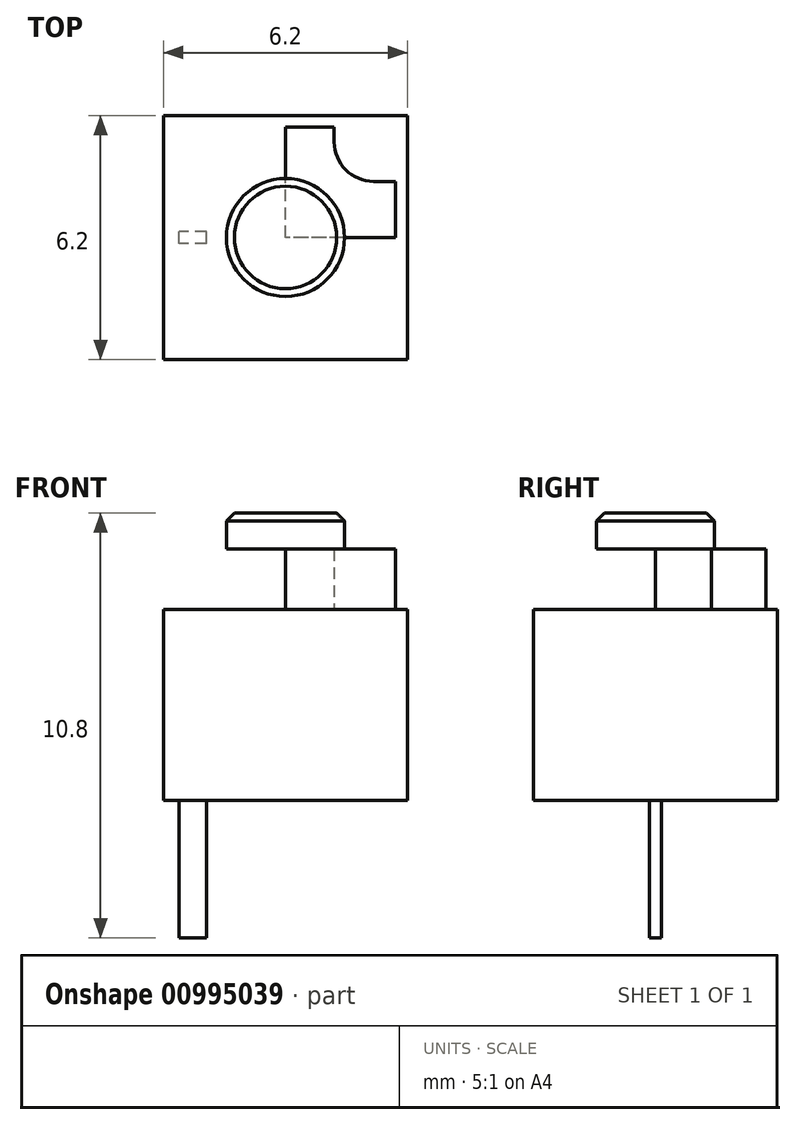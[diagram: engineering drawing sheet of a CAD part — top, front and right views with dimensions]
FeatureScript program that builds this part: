
annotation { "Feature Type Name" : "Feature", "Feature Type Description" : "" }
export const myFeature = defineFeature(function(context is Context, id is Id, definition is map)
    precondition{}
    {
        {
            var Q0;
            Q0=qCreatedBy(makeId("Top.planeOp"),FACE);
            var sketch = newSketch(context, id + "F0", { "sketchPlane" : qUnion([Q0])});
            skLineSegment(sketch, "E0.bottom", {"start": v(3.1, 3.1) * mm, "end": v(-3.1, 3.1) * mm});
            skLineSegment(sketch, "E0.top", {"start": v(3.1, -3.1) * mm, "end": v(-3.1, -3.1) * mm});
            skLineSegment(sketch, "E0.left", {"start": v(3.1, 3.1) * mm, "end": v(3.1, -3.1) * mm});
            skLineSegment(sketch, "E0.right", {"start": v(-3.1, 3.1) * mm, "end": v(-3.1, -3.1) * mm});
            skPoint(sketch, "E0.middle", {"position": v(0, 0) * mm});
            skSolve(sketch);
        }
        {
            var Q0;
            Q0=qSketchRegion(id+"F0",true);
            extrude(context, id + "F1", {"entities" : qUnion([Q0]), "depth" : 4.85 * mm, "offsetDistance" : 25 * mm});
        }
        {
            var Q0;
            Q0=makeQuery(id+"F1.opExtrude","CAP_FACE",FACE,{"disambiguationData":[OSD([sQuery(id+"F0.wireOp",EDGE,"E0.bottom"),sQuery(id+"F0.wireOp",EDGE,"E0.top"),sQuery(id+"F0.wireOp",EDGE,"E0.left"),sQuery(id+"F0.wireOp",EDGE,"E0.right")])],"isStart":false});
            var sketch = newSketch(context, id + "F2", { "sketchPlane" : qUnion([Q0])});
            skLineSegment(sketch, "E1", {"start": v(0, 2.8) * mm, "end": v(1.24, 2.8) * mm});
            skLineSegment(sketch, "E2", {"start": v(1.24, 2.8) * mm, "end": v(1.24, 2.43) * mm});
            skLineSegment(sketch, "E3", {"start": v(2.24, 1.43) * mm, "end": v(2.8, 1.43) * mm});
            skLineSegment(sketch, "E4", {"start": v(2.8, 1.43) * mm, "end": v(2.8, 0) * mm});
            skLineSegment(sketch, "E5", {"start": v(2.8, 0) * mm, "end": v(0, 0) * mm});
            skLineSegment(sketch, "E6", {"start": v(0, 0) * mm, "end": v(0, 2.8) * mm});
            skPoint(sketch, "E7.visualSharp", {"position": v(1.24, 1.43) * mm});
            skArc(sketch, "E7.filletArc", {"start": v(1.24, 2.43) * mm, "mid": v(1.53, 1.72) * mm, "end": v(2.24, 1.43) * mm});
            skSolve(sketch);
        }
        {
            var Q0;
            Q0=qSketchRegion(id+"F2",true);
            extrude(context, id + "F3", {"entities" : qUnion([Q0]), "operationType" : NewBodyOperationType.ADD, "depth" : (6.38 - 4.85) * mm, "offsetDistance" : 25 * mm});
        }
        {
            var Q0;
            {var subQ0=sQuery(id+"F2.wireOp",EDGE,"E7.filletArc");var subQ1=sQuery(id+"F2.wireOp",EDGE,"E6");var subQ2=sQuery(id+"F2.wireOp",EDGE,"E5");var subQ3=sQuery(id+"F2.wireOp",EDGE,"E4");var subQ4=sQuery(id+"F2.wireOp",EDGE,"E3");var subQ5=sQuery(id+"F2.wireOp",EDGE,"E2");var subQ6=sQuery(id+"F2.wireOp",EDGE,"E1");Q0=makeQuery(id+"Flg9rYBYSU9C4zM_1.3.F3.boolean.opBoolean","MERGE",FACE,{"derivedFrom":[makeQuery(id+"Flg9rYBYSU9C4zM_1.2.F3.boolean.opBoolean","MERGE",FACE,{"derivedFrom":[makeQuery(id+"Flg9rYBYSU9C4zM_1.1.F3.boolean.opBoolean","MERGE",FACE,{"derivedFrom":[makeQuery(id+"F3.opExtrude","CAP_FACE",FACE,{"disambiguationData":[OSD([subQ6,subQ5,subQ4,subQ3,subQ2,subQ1,subQ0])],"isStart":false}),makeQuery(id+"Flg9rYBYSU9C4zM_1.1.F3.opExtrude","CAP_FACE",FACE,{"disambiguationData":[OSD([subQ6,subQ5,subQ4,subQ3,subQ2,subQ1,subQ0])],"isStart":false})]}),makeQuery(id+"Flg9rYBYSU9C4zM_1.2.F3.opExtrude","CAP_FACE",FACE,{"disambiguationData":[OSD([subQ6,subQ5,subQ4,subQ3,subQ2,subQ1,subQ0])],"isStart":false})]}),makeQuery(id+"Flg9rYBYSU9C4zM_1.3.F3.opExtrude","CAP_FACE",FACE,{"disambiguationData":[OSD([subQ6,subQ5,subQ4,subQ3,subQ2,subQ1,subQ0])],"isStart":false})]});}
            var sketch = newSketch(context, id + "F4", { "sketchPlane" : qUnion([Q0])});
            skCircle(sketch, "E8", {"center": v(0, 0) * mm, "radius": 1.5 * mm});
            skSolve(sketch);
        }
        {
            var Q0;
            Q0=qSketchRegion(id+"F4",true);
            extrude(context, id + "F5", {"entities" : qUnion([Q0]), "operationType" : NewBodyOperationType.ADD, "depth" : (7.3 - 6.38) * mm, "offsetDistance" : 25 * mm});
        }
        {
            var Q0;
            Q0=makeQuery(id+"F5.opExtrude","CAP_EDGE",EDGE,{"disambiguationData":[OSD([sQuery(id+"F4.wireOp",EDGE,"E8")])],"isStart":false});
            chamfer(context, id + "F6", {"entities" : qUnion([Q0]), "width" : 0.2 * mm, "tangentPropagation" : true});
        }
        {
            var Q0;
            Q0=qCreatedBy(makeId("Front.planeOp"),FACE);
            var sketch = newSketch(context, id + "F7", { "sketchPlane" : qUnion([Q0])});
            skLineSegment(sketch, "E9", {"start": v(-2.7, 0) * mm, "end": v(-2.7, -3.5) * mm});
            skLineSegment(sketch, "E10", {"start": v(-2.7, -3.5) * mm, "end": v(-2, -3.5) * mm});
            skLineSegment(sketch, "E11", {"start": v(-2, -3.5) * mm, "end": v(-2, 0) * mm});
            skLineSegment(sketch, "E12", {"start": v(-2, 0) * mm, "end": v(-2.7, 0) * mm});
            skPoint(sketch, "E13", {"position": v(-2.35, 0) * mm});
            skSolve(sketch);
        }
        {
            var Q0;
            Q0=qSketchRegion(id+"F7",true);
            extrude(context, id + "F8", {"entities" : qUnion([Q0]), "operationType" : NewBodyOperationType.ADD, "endBound" : BoundingType.SYMMETRIC, "depth" : 0.3 * mm, "offsetDistance" : 25 * mm});
        }
    });
